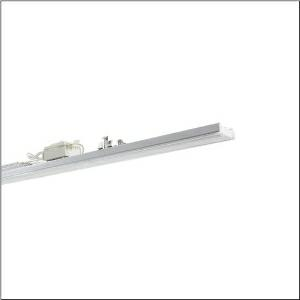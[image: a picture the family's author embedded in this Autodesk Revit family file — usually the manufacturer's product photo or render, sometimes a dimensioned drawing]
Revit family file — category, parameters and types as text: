
# Revit family: licross_21_recessed_mo_52tl18vn565g
name_source: partatom
category: Lighting Fixtures
units: mm (PartAtom-declared; Revit-internal decimal feet)

## family parameters
Cut with Voids When Loaded = No
Host = Face
Light Source = No
Part Type = Normal
Room Calculation Point = No
Round Connector Dimension = Use Diameter
Shared = No

## types (1)
- --- (1 x LED, 6500 lm, 37.3 W, 5000K)
    Apparent Load = 37 VA
    CIE Flux Codes = 79 95 99 100 100
    Color Rendering = 80
    Color Temperature = 5000K
    Default Elevation = 1800 mm
    Description = Licross 21 Recessed MO, luminaire insert, of sheet steel, galvanised, coil coated, white, length: 1.500mm, width: 66mm, height: 67mm, LED rated luminous flux: 6.500lm, light colour: 850, SDCM (Standard Deviation of Colour Matching)MacAdam ≤ 3 SDCM (initial), control gear: DALI 2, CLO, with plug, 5-pole, with phase selection, mains connection: 220..240V, AC, 50/60Hz, start of lifetime: 37W, end of service life: 44W, internal wiring halogen-free, primary optical cover: cover, of PMMA, light emission: direct distribution, primary light characteristic: symmetric, protection rating (complete): IP40, insulation class (complete): insulation class I (protective earthing), certification: CE, ENEC, VDE, UKCA, protection symbol: D if used in an environment without relevant dust loads with corresponding accessories, impact resistance: IK06, permissible ambient temperature for indoor applications: -25..+40°C, corresponds to IFS (International Featured Standards) requirements for safety and quality in the food industry, reducing of maximum allowable ambient temperature of 5°C with ceiling mounting, LABS conformity tested according to VDMA 24364:2018-05, The light source and the operating device comply with the requirements of the Ecodesign Regulation (EU) 2019/2020 and are replaceable in accordance with this regulation, packaging unit: 1 piece
    Height = 58 mm
    Lamp = 1 x LED
    Lamp Light Flux = 6500 lm
    Lamp Power = 37.3 W
    Lamp count = 1
    Length = 1500 mm
    Luminous efficacy = 174 lm/W
    Manufacturer = Siteco
    ModVariant = No
    Model = 52TL18VN565G
    Mounting Place = Ceiling
    Mounting Type = Pendant
    Number of Poles = 1
    OnlyDefault = Yes
    Power Factor = 1
    Product Name = Licross 21 Recessed MO
    Product group = luminaire insert | ceiling pendant
    ProductGroupID = 901
    Protection Class = Protection class I
    Protection Degree = IP 40
    RLX_Detail_Level = 1
    RLX_Emergency_Light_Flux = 0 lm
    RLX_Emergency_Type = 0
    RLX_Emergency_Type_DB = No
    RlxData = <blob elided: 24805 chars, md5=bfc5f234>
    Socket = socket
    Standby Power = 0 W
    System Light Flux = 6500 lm
    System Power = 37 W
    Type Comments = factory setting: luminous flux: 100 % | dim-lin: 254 | 249 mA
    Type Image = l_1296930.jpg
    URL = http://relux.com
    VarID = @adj_087161
    Voltage = 0 V
    Weight = 0.00 kg
    Width = 66 mm

## geometry (parser evidence)
native form markers: Blend x4, Sweep x9
no freeform markers — native parametric forms only
